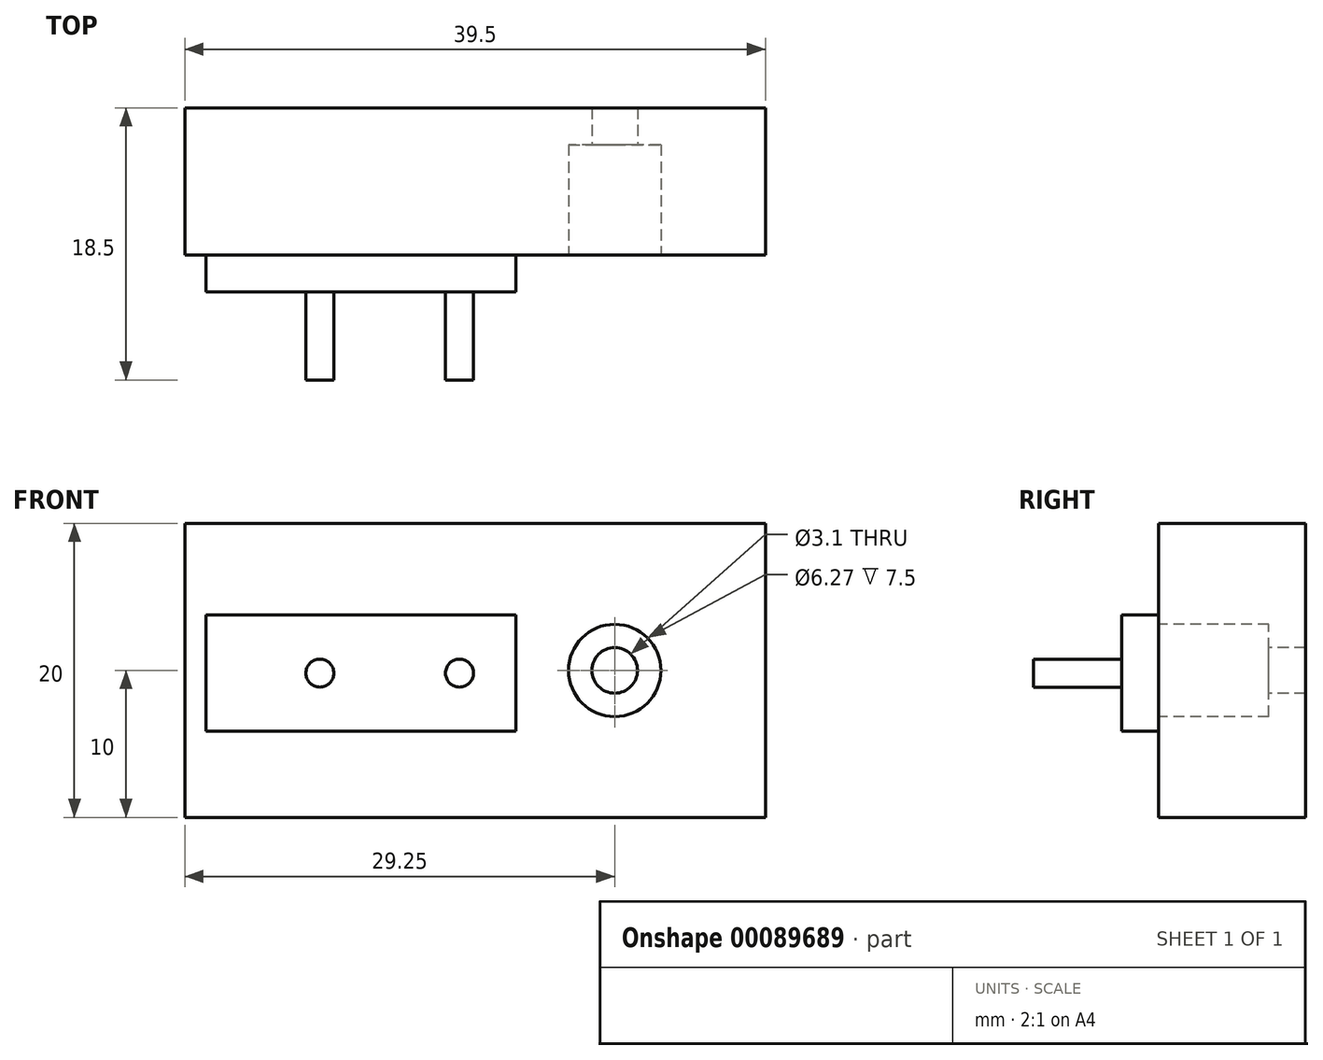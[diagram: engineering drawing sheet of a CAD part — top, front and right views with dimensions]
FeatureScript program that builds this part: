
annotation { "Feature Type Name" : "Feature", "Feature Type Description" : "" }
export const myFeature = defineFeature(function(context is Context, id is Id, definition is map)
    precondition{}
    {
        {
            var Q0;
            Q0=qCreatedBy(makeId("Front.planeOp"),FACE);
            var sketch = newSketch(context, id + "F0", { "sketchPlane" : qUnion([Q0])});
            skLineSegment(sketch, "E0.bottom", {"start": v(0, 0) * mm, "end": v(39.5, 0) * mm});
            skLineSegment(sketch, "E0.top", {"start": v(0, 20) * mm, "end": v(39.5, 20) * mm});
            skLineSegment(sketch, "E0.left", {"start": v(0, 0) * mm, "end": v(0, 20) * mm});
            skLineSegment(sketch, "E0.right", {"start": v(39.5, 0) * mm, "end": v(39.5, 20) * mm});
            skSolve(sketch);
        }
        {
            var Q0;
            Q0=makeQuery(id+"F0.imprint","IMPRINT",FACE,{"disambiguationData":[TD([[makeQuery(id+"F0.imprint","IMPRINT",EDGE,{"derivedFrom":sQuery(id+"F0.wireOp",EDGE,"E0.bottom")}),1.0]])]});
            extrude(context, id + "F1", {"entities" : qUnion([Q0]), "depth" : 10 * mm});
        }
        {
            var Q0;
            Q0=makeQuery(id+"F1.opExtrude","CAP_FACE",FACE,{"disambiguationData":[OSD([sQuery(id+"F0.wireOp",EDGE,"E0.bottom"),sQuery(id+"F0.wireOp",EDGE,"E0.top"),sQuery(id+"F0.wireOp",EDGE,"E0.left"),sQuery(id+"F0.wireOp",EDGE,"E0.right")])],"isStart":false});
            var sketch = newSketch(context, id + "F2", { "sketchPlane" : qUnion([Q0])});
            skLineSegment(sketch, "E1", {"start": v(39.5, 10) * mm, "end": v(29.25, 10) * mm});
            skPoint(sketch, "E1.endSnap0", {"position": v(39.5, 10) * mm});
            skCircle(sketch, "E2", {"center": v(29.25, 10) * mm, "radius": 1.55 * mm});
            skSolve(sketch);
        }
        {
            var Q0;
            Q0=makeQuery(id+"F2.imprint","IMPRINT",FACE,{"disambiguationData":[TD([[makeQuery(id+"F2.imprint","IMPRINT",EDGE,{"derivedFrom":sQuery(id+"F2.wireOp",EDGE,"E2")}),1.0]])]});
            extrude(context, id + "F3", {"entities" : qUnion([Q0]), "operationType" : NewBodyOperationType.REMOVE, "oppositeDirection" : true, "depth" : 25 * mm});
        }
        {
            var Q0;
            Q0=makeQuery(id+"F1.opExtrude","CAP_FACE",FACE,{"disambiguationData":[OSD([sQuery(id+"F0.wireOp",EDGE,"E0.bottom"),sQuery(id+"F0.wireOp",EDGE,"E0.top"),sQuery(id+"F0.wireOp",EDGE,"E0.left"),sQuery(id+"F0.wireOp",EDGE,"E0.right")])],"isStart":false});
            var sketch = newSketch(context, id + "F4", { "sketchPlane" : qUnion([Q0])});
            skLineSegment(sketch, "E3.bottom", {"start": v(1.45, 5.88) * mm, "end": v(22.53, 5.88) * mm});
            skLineSegment(sketch, "E3.top", {"start": v(1.45, 13.76) * mm, "end": v(22.53, 13.76) * mm});
            skLineSegment(sketch, "E3.left", {"start": v(1.45, 5.88) * mm, "end": v(1.45, 13.76) * mm});
            skLineSegment(sketch, "E3.right", {"start": v(22.53, 5.88) * mm, "end": v(22.53, 13.76) * mm});
            skSolve(sketch);
        }
        {
            var Q0;
            Q0=makeQuery(id+"F4.imprint","IMPRINT",FACE,{"disambiguationData":[TD([[makeQuery(id+"F4.imprint","IMPRINT",EDGE,{"derivedFrom":sQuery(id+"F4.wireOp",EDGE,"E3.bottom")}),1.0]])]});
            extrude(context, id + "F5", {"entities" : qUnion([Q0]), "operationType" : NewBodyOperationType.ADD, "depth" : 2.5 * mm});
        }
        {
            var Q0;
            Q0=makeQuery(id+"F5.opExtrude","CAP_FACE",FACE,{"disambiguationData":[OSD([sQuery(id+"F4.wireOp",EDGE,"E3.bottom"),sQuery(id+"F4.wireOp",EDGE,"E3.top"),sQuery(id+"F4.wireOp",EDGE,"E3.left"),sQuery(id+"F4.wireOp",EDGE,"E3.right")])],"isStart":false});
            var sketch = newSketch(context, id + "F6", { "sketchPlane" : qUnion([Q0])});
            skLineSegment(sketch, "E4", {"start": v(1.45, 9.82) * mm, "end": v(9.2, 9.82) * mm});
            skLineSegment(sketch, "E5", {"start": v(9.2, 9.82) * mm, "end": v(18.7, 9.82) * mm});
            skLineSegment(sketch, "E6", {"start": v(18.7, 9.82) * mm, "end": v(22.53, 9.82) * mm});
            skCircle(sketch, "E7", {"center": v(9.2, 9.82) * mm, "radius": 0.95 * mm});
            skCircle(sketch, "E8", {"center": v(18.7, 9.82) * mm, "radius": 0.95 * mm});
            skSolve(sketch);
        }
        {
            var Q0;
            {var subQ0=sQuery(id+"F6.wireOp",EDGE,"E6");var subQ1=sQuery(id+"F6.wireOp",EDGE,"E5");var subQ2=makeQuery(id+"F6.imprint","INTERSECT",VERTEX,{"derivedFrom":[subQ1,subQ0]});Q0=makeQuery(id+"F6.imprint","IMPRINT",FACE,{"disambiguationData":[TD([[makeQuery(id+"F6.imprint","IMPRINT",EDGE,{"disambiguationData":[TD([[subQ2,1.0]])],"derivedFrom":subQ1}),-1.0]])]});}
            var Q1;
            {var subQ0=sQuery(id+"F6.wireOp",EDGE,"E6");var subQ1=sQuery(id+"F6.wireOp",EDGE,"E5");var subQ2=makeQuery(id+"F6.imprint","INTERSECT",VERTEX,{"derivedFrom":[subQ1,subQ0]});Q1=makeQuery(id+"F6.imprint","IMPRINT",FACE,{"disambiguationData":[TD([[makeQuery(id+"F6.imprint","IMPRINT",EDGE,{"disambiguationData":[TD([[subQ2,1.0]])],"derivedFrom":subQ1}),1.0]])]});}
            var Q2;
            {var subQ0=sQuery(id+"F6.wireOp",EDGE,"E5");var subQ1=sQuery(id+"F6.wireOp",EDGE,"E4");var subQ2=makeQuery(id+"F6.imprint","INTERSECT",VERTEX,{"derivedFrom":[subQ1,subQ0]});Q2=makeQuery(id+"F6.imprint","IMPRINT",FACE,{"disambiguationData":[TD([[makeQuery(id+"F6.imprint","IMPRINT",EDGE,{"disambiguationData":[TD([[subQ2,1.0]])],"derivedFrom":subQ1}),1.0]])]});}
            var Q3;
            {var subQ0=sQuery(id+"F6.wireOp",EDGE,"E5");var subQ1=sQuery(id+"F6.wireOp",EDGE,"E4");var subQ2=makeQuery(id+"F6.imprint","INTERSECT",VERTEX,{"derivedFrom":[subQ1,subQ0]});Q3=makeQuery(id+"F6.imprint","IMPRINT",FACE,{"disambiguationData":[TD([[makeQuery(id+"F6.imprint","IMPRINT",EDGE,{"disambiguationData":[TD([[subQ2,1.0]])],"derivedFrom":subQ1}),-1.0]])]});}
            extrude(context, id + "F7", {"entities" : qUnion([Q0, Q1, Q2, Q3]), "operationType" : NewBodyOperationType.ADD, "depth" : 6 * mm});
        }
        {
            var Q0;
            Q0=makeQuery(id+"F1.opExtrude","CAP_FACE",FACE,{"disambiguationData":[OSD([sQuery(id+"F0.wireOp",EDGE,"E0.bottom"),sQuery(id+"F0.wireOp",EDGE,"E0.top"),sQuery(id+"F0.wireOp",EDGE,"E0.left"),sQuery(id+"F0.wireOp",EDGE,"E0.right")])],"isStart":false});
            var sketch = newSketch(context, id + "F8", { "sketchPlane" : qUnion([Q0])});
            skCircle(sketch, "E9", {"center": v(29.25, 10) * mm, "radius": 3.14 * mm});
            skSolve(sketch);
        }
        {
            var Q0;
            Q0=makeQuery(id+"F8.imprint","IMPRINT",FACE,{"disambiguationData":[TD([[makeQuery(id+"F8.imprint","IMPRINT",EDGE,{"derivedFrom":sQuery(id+"F8.wireOp",EDGE,"E9")}),1.0]])]});
            extrude(context, id + "F9", {"entities" : qUnion([Q0]), "operationType" : NewBodyOperationType.REMOVE, "oppositeDirection" : true, "depth" : 7.5 * mm});
        }
    });
